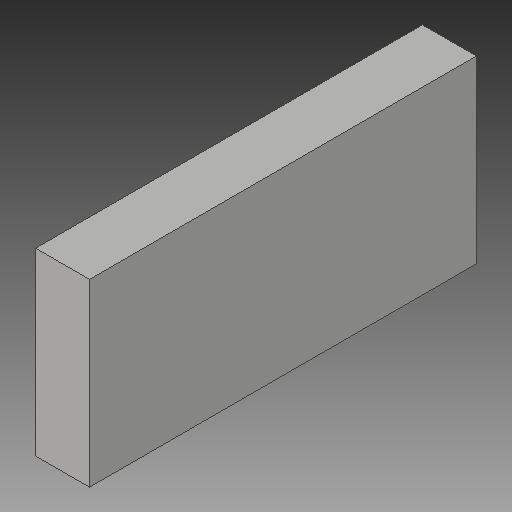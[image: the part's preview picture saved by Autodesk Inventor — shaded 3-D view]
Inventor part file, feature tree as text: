
AUTODESK INVENTOR PART (.ipt)
format: ipt  version: 2018 (Build 220112000, 112)  size: 105,984 bytes
history: native  units: mm
features: thread x4, extrude x3, sketch x3
ambient origin geometry x8: Origin, YZ Plane, XZ Plane, XY Plane, X Axis, Y Axis, Z Axis, Center Point
bodies: Solid1 (feature_tree)
feature tree (10):
  extrude  "Extrusion1"  Depth=86.0mm
  extrude  "Extrusion2"  Depth=12.0mm
  extrude  "Extrusion3"  Depth=10.0mm
  thread  "Thread1"  [1 undecoded]
  thread  "Thread2"  [1 undecoded]
  thread  "Thread3"  [1 undecoded]
  thread  "Thread4"  [1 undecoded]
  sketch  "Sketch1"  dims[d0=40.0mm d1=86.0mm]
  sketch  "Sketch2"  dims[d2=12.0mm d3=0.0mm d4=6.0mm]
  sketch  "Sketch3"  dims[d6=10.0mm d7=20.0mm d8=15.0mm d9=0.0mm d10=6.0mm d11=10.0mm d12=20.0mm d13=15.0mm d14=0.0mm d15=10.0mm d16=0.0mm d17=10.0mm d18=0.0mm d19=10.0mm d20=0.0mm d21=10.0mm d22=0.0mm]
note: 4 required parameter values undecoded (feature->parameter linkage not recoverable at this tier; creation-order binding heuristic only, values carry confidence <= 0.55)
